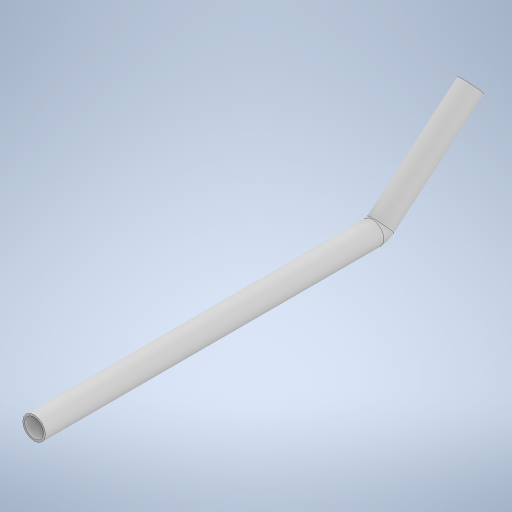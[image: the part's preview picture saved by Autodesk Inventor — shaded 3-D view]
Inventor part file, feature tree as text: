
AUTODESK INVENTOR PART (.ipt)
format: ipt  version: 2024 (Build 280153000, 153)  size: 256,512 bytes
history: native  units: in
note: dims shown in document units (in); Inventor stores cm internally (conversion verified against a paired STEP export)
features: sketch x2, extrude x1, plane x1, other x1
ambient origin geometry x8: Origin, YZ Plane, XZ Plane, XY Plane, X Axis, Y Axis, Z Axis, Center Point
bodies: Solid1 (feature_tree)
feature tree (5):
  extrude  "Extrusion1"  Depth=0.7874in
  plane  "Work Plane1"
  other  "Bend Part1"
  sketch  "Sketch1"  dims[d0=0.9449in d1=0.7874in]
  sketch  "Sketch2"  dims[d2=19.685in d3=0.0in d4=5.5906in d5=1.0in d6=0.2749in]
